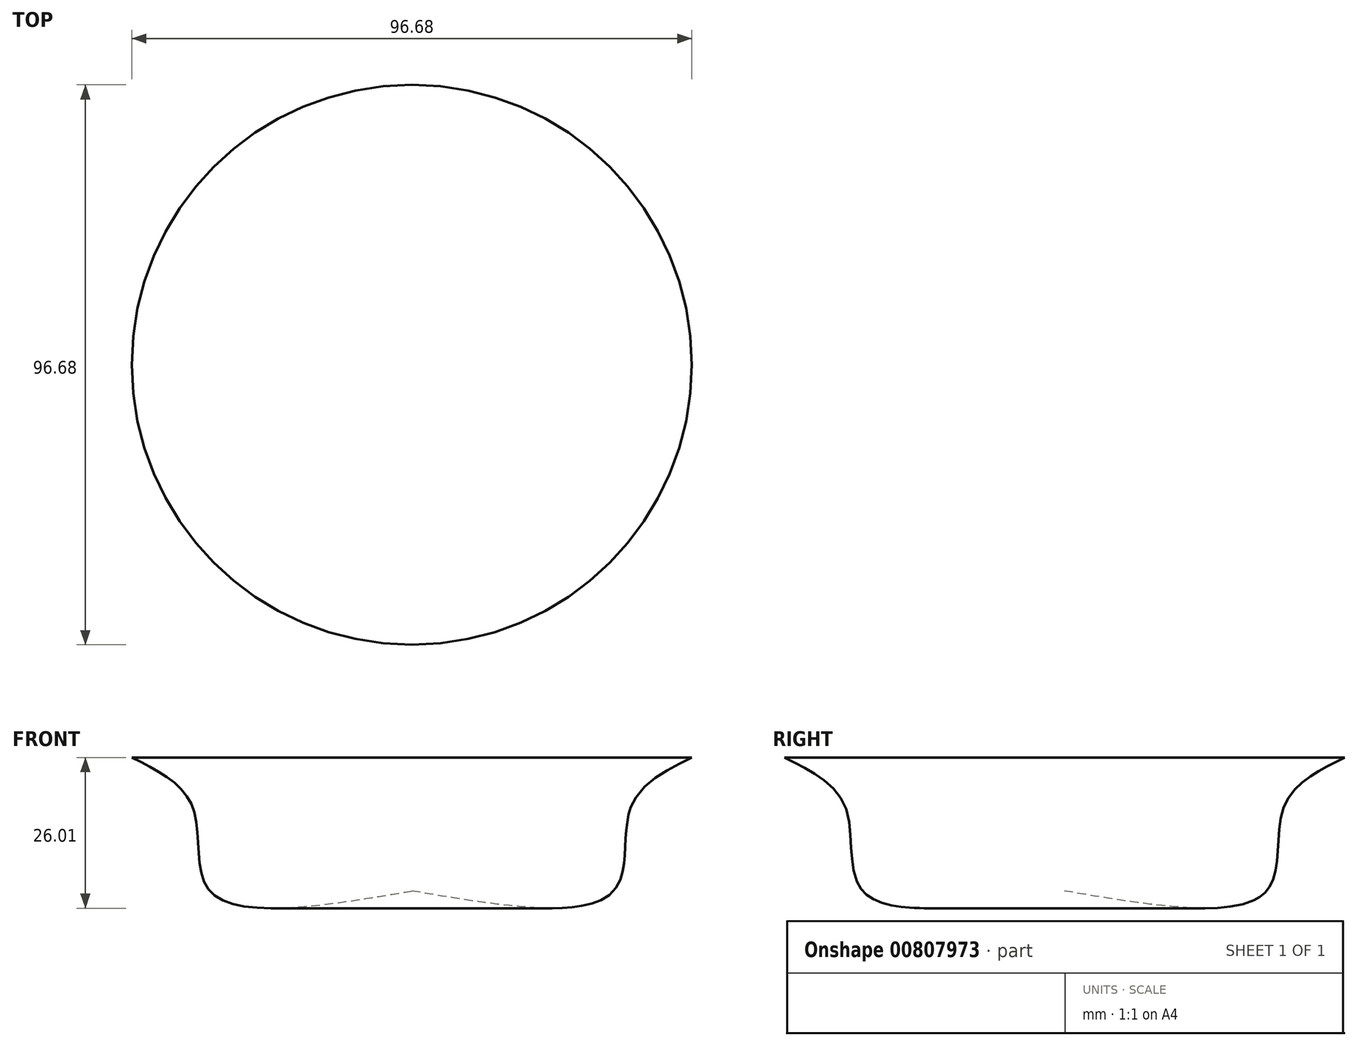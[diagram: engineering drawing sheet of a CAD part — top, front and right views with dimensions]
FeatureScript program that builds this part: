
annotation { "Feature Type Name" : "Feature", "Feature Type Description" : "" }
export const myFeature = defineFeature(function(context is Context, id is Id, definition is map)
    precondition{}
    {
        {
            var Q0;
            Q0=qCreatedBy(makeId("Front.planeOp"),FACE);
            var sketch = newSketch(context, id + "F0", { "sketchPlane" : qUnion([Q0])});
            skFitSpline(sketch, "E0", {"points": [v(-48.34, 23.03) * mm, v(-37.76, 14.31) * mm, v(-34.85, 0) * mm, v(0, 0) * mm], "startDerivative": vector(49.18, -24.2) * mm, "endDerivative": vector(103.62, 17.58) * mm});
            skLineSegment(sketch, "E1", {"start": v(0, 0) * mm, "end": v(0, 23.03) * mm});
            skSolve(sketch);
        }
        {
            var Q0;
            Q0=sQuery(id+"F0.wireOp",EDGE,"E0");
            var Q1;
            Q1=sQuery(id+"F0.wireOp",EDGE,"E1");
            revolve(context, id + "F1", {"bodyType" : ToolBodyType.SURFACE, "surfaceOperationType" : NewSurfaceOperationType.NEW, "surfaceEntities" : qUnion([Q0]), "axis" : qUnion([Q1]), "revolveType" : RevolveType.FULL});
        }
    });
